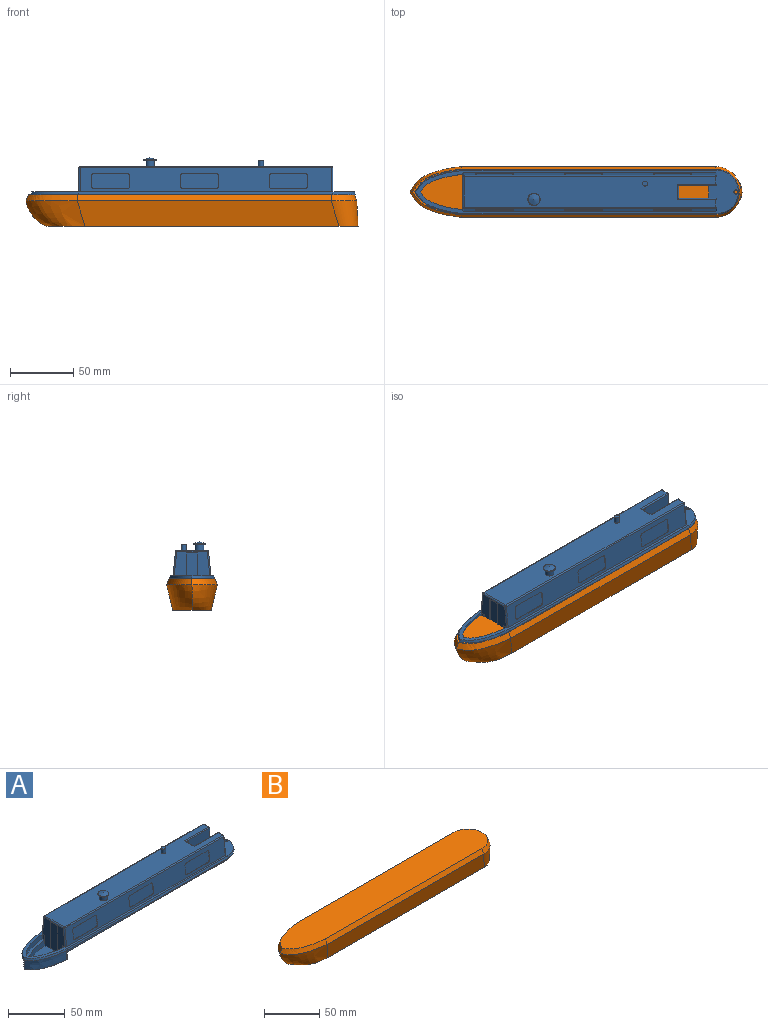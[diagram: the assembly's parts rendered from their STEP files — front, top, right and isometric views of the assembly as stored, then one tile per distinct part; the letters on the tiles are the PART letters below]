
ASSEMBLY  parts=2 mates=1
PART A: 146 faces, bbox 258.2x37.5x42 mm
  f0: plane 214.33x14.24mm, normal (0,0,-1), area 43.4mm2, adj f37,f39,f111,f132,f136,f137
  f1: plane 214.36x14.27mm, normal (0,0,-1), area 43.2mm2, adj f38,f40,f111,f132,f134,f135
  f2: plane 198.05x19.1mm, normal (0,0.99,0.1), area 2766.1mm2, adj f11,f82,f83,f84,f85,f86,f87,f88
  f3: plane 198.05x19.1mm, normal (0,-0.99,0.1), area 2734.1mm2, adj f11,f55,f56,f57,f58,f59,f60,f61
  f4: plane 20x1.2mm, normal (-1,0,0), area 24mm2, adj f6,f36,f44,f52
  f5: plane 198.05x24.04mm, normal (0,0,1), area 4345.1mm2, adj f117,f122,f123,f127,f128,f129,f130,f131
  f6: plane 197.65x23.68mm, normal (0,0,-1), area 4327.5mm2, adj f4,f7,f35,f36,f41,f42,f43,f49
  f7: plane 20x1.2mm, normal (-1,0,0), area 24mm2, adj f6,f35,f44,f51
  f8: plane 19x8.91mm, normal (1,0,0), area 150.5mm2, adj f11,f36,f121,f127
  f9: plane 19x8.91mm, normal (1,0,0), area 150.5mm2, adj f11,f35,f124,f128
  f10: plane 30x27.99mm, normal (-1,0,0), area 473mm2, adj f11,f12,f22,f23,f112,f113,f114,f116
  f11: plane 254.58x34.49mm, normal (0,0,1), area 1551.4mm2, adj f2,f3,f8,f9,f10,f12,f22,f24
  f12: extruded ~29.98x11mm, area 198mm2, adj f10,f11,f22,f23,f30,f34
  f13: plane 256.13x35.95mm, normal (0,0,-1), area 894.4mm2, adj f14,f15,f16,f17,f18,f19,f24,f25
  f14: extruded ~36.01x16mm, area 451.2mm2, adj f13,f15,f19,f139
  f15: extruded ~36.01x16mm, area 451.2mm2, adj f13,f14,f16,f138
  f16: plane 199.94x11.11mm, normal (0,-1,0), area 607.9mm2, adj f13,f15,f17,f111,f135,f138
  f17: extruded ~15.98x15.13mm, area 72.8mm2, adj f13,f16,f132,f134
  f18: extruded ~15.98x15.13mm, area 72.8mm2, adj f13,f19,f132,f137
  f19: plane 199.94x11.11mm, normal (0,1,0), area 607.9mm2, adj f13,f14,f18,f111,f136,f139
  f20: plane 24.6x0.09mm, normal (0,0,-1), area 2.1mm2, adj f43,f45,f46,f111
  f21: plane 36.84x31.2mm, normal (0,0,-1), area 770.6mm2, adj f111,f138,f139
  f22: extruded ~29.98x11mm, area 198mm2, adj f10,f11,f12,f23,f31,f34
  f23: plane 30.48x21.91mm, normal (0,0,1), area 454.3mm2, adj f10,f12,f22,f112,f113,f115
  f24: plane 200.04x2mm, normal (0,0.95,0.32), area 421.7mm2, adj f11,f13,f25,f26
  f25: bspline ~18.01x18mm, area 57.4mm2, adj f11,f13,f24,f27
  f26: bspline ~41.47x20.63mm, area 90.8mm2, adj f11,f13,f24,f28
  f27: bspline ~18.01x18mm, area 57.4mm2, adj f11,f13,f25,f29
  f28: bspline ~41.47x20.63mm, area 90.8mm2, adj f11,f13,f26,f29
  f29: plane 200.04x2mm, normal (0,-0.95,0.32), area 421.7mm2, adj f11,f13,f27,f28
  f30: plane 5x3.02mm, normal (-1,0,0), area 15.1mm2, adj f11,f12,f33,f34
  f31: plane 5x3.02mm, normal (-1,0,0), area 15.1mm2, adj f11,f22,f32,f34
  f32: extruded ~33.25x13.94mm, area 186.5mm2, adj f11,f31,f33,f34
  f33: extruded ~33.25x13.94mm, area 186.5mm2, adj f11,f30,f32,f34
  f34: plane 33.25x27.88mm, normal (0,0,1), area 209mm2, adj f12,f22,f30,f31,f32,f33
  f35: plane 30x20.2mm, normal (0,-1,0), area 522.4mm2, adj f6,f7,f9,f11,f44,f53,f54,f130
  f36: plane 30x20.2mm, normal (0,1,0), area 522.4mm2, adj f4,f6,f8,f11,f44,f53,f54,f129
  f37: plane 199.19x4.8mm, normal (0,-1,0), area 956.1mm2, adj f0,f39,f44,f48,f109
  f38: plane 199.19x4.8mm, normal (0,1,0), area 956.1mm2, adj f1,f40,f44,f47,f110
  f39: extruded ~14.75x13.59mm, area 105.8mm2, adj f0,f37,f44,f132
  f40: extruded ~14.75x13.59mm, area 105.8mm2, adj f1,f38,f44,f132
  f41: plane 20x7.63mm, normal (-1,0,0), area 131.8mm2, adj f6,f44,f49,f52
  f42: plane 20x7.63mm, normal (-1,0,0), area 131.8mm2, adj f6,f44,f50,f51
  f43: plane 27.84x24.8mm, normal (1,0,0), area 633.2mm2, adj f6,f20,f44,f45,f46,f49,f50
  f44: plane 214.42x30.07mm, normal (0,0,-1), area 840.3mm2, adj f4,f7,f35,f36,f37,f38,f39,f40
  f45: extruded ~4.8x0.34mm, area 1.7mm2, adj f20,f43,f44,f47,f110
  f46: extruded ~4.8x0.34mm, area 1.7mm2, adj f20,f43,f44,f48,f109
  f47: plane 4.8x2.54mm, normal (1,0,0), area 12.2mm2, adj f38,f44,f45,f110
  f48: plane 4.8x2.54mm, normal (1,0,0), area 12.2mm2, adj f37,f44,f46,f109
  f49: plane 197.65x20mm, normal (0,0.99,-0.1), area 3974.3mm2, adj f6,f41,f43,f44
  f50: plane 197.65x20mm, normal (0,-0.99,-0.1), area 3974.3mm2, adj f6,f42,f43,f44
  f51: plane 25x20mm, normal (0,1,0), area 500mm2, adj f6,f7,f42,f44
  f52: plane 25x20mm, normal (0,-1,0), area 500mm2, adj f4,f6,f41,f44
  f53: plane 10.17x0.2mm, normal (1,0,0), area 2mm2, adj f6,f35,f36,f131
  f54: plane 10.17x1.2mm, normal (-1,0,0), area 12.2mm2, adj f11,f35,f36,f44
  f55: plane 8.01x1.32mm, normal (-1,0,0), area 4mm2, adj f3,f56,f62,f63
  f56: cylinder r=2mm len=2.04mm, axis (0,-0.99,0.1), area 1.6mm2, adj f3,f55,f57,f63
  f57: plane 26x0.5mm, normal (0,-0.1,-0.99), area 13mm2, adj f3,f56,f58,f63
  f58: cylinder r=2mm len=2.04mm, axis (0,-0.99,0.1), area 1.6mm2, adj f3,f57,f59,f63
  f59: plane 8.01x1.32mm, normal (1,0,0), area 4mm2, adj f3,f58,f60,f63
  f60: cylinder r=2mm len=2.04mm, axis (0,-0.99,0.1), area 1.6mm2, adj f3,f59,f61,f63
  f61: plane 26x0.5mm, normal (0,0.1,0.99), area 13mm2, adj f3,f60,f62,f63
  f62: cylinder r=2mm len=2.04mm, axis (0,-0.99,0.1), area 1.6mm2, adj f3,f55,f61,f63
  f63: plane 30x11.94mm, normal (0,-0.99,0.1), area 356.6mm2, adj f55,f56,f57,f58,f59,f60,f61,f62
  f64: plane 8.01x1.32mm, normal (-1,0,0), area 4mm2, adj f3,f65,f71,f72
  f65: cylinder r=2mm len=2.04mm, axis (0,-0.99,0.1), area 1.6mm2, adj f3,f64,f66,f72
  f66: plane 26x0.5mm, normal (0,-0.1,-0.99), area 13mm2, adj f3,f65,f67,f72
  f67: cylinder r=2mm len=2.04mm, axis (0,-0.99,0.1), area 1.6mm2, adj f3,f66,f68,f72
  f68: plane 8.01x1.32mm, normal (1,0,0), area 4mm2, adj f3,f67,f69,f72
  f69: cylinder r=2mm len=2.04mm, axis (0,-0.99,0.1), area 1.6mm2, adj f3,f68,f70,f72
  f70: plane 26x0.5mm, normal (0,0.1,0.99), area 13mm2, adj f3,f69,f71,f72
  f71: cylinder r=2mm len=2.04mm, axis (0,-0.99,0.1), area 1.6mm2, adj f3,f64,f70,f72
  f72: plane 30x11.94mm, normal (0,-0.99,0.1), area 356.6mm2, adj f64,f65,f66,f67,f68,f69,f70,f71
  f73: plane 8.01x1.32mm, normal (-1,0,0), area 4mm2, adj f3,f74,f80,f81
  f74: cylinder r=2mm len=2.04mm, axis (0,-0.99,0.1), area 1.6mm2, adj f3,f73,f75,f81
  f75: plane 26x0.5mm, normal (0,-0.1,-0.99), area 13mm2, adj f3,f74,f76,f81
  f76: cylinder r=2mm len=2.04mm, axis (0,-0.99,0.1), area 1.6mm2, adj f3,f75,f77,f81
  f77: plane 8.01x1.32mm, normal (1,0,0), area 4mm2, adj f3,f76,f78,f81
  f78: cylinder r=2mm len=2.04mm, axis (0,-0.99,0.1), area 1.6mm2, adj f3,f77,f79,f81
  f79: plane 26x0.5mm, normal (0,0.1,0.99), area 13mm2, adj f3,f78,f80,f81
  f80: cylinder r=2mm len=2.04mm, axis (0,-0.99,0.1), area 1.6mm2, adj f3,f73,f79,f81
  f81: plane 30x11.94mm, normal (0,-0.99,0.1), area 356.6mm2, adj f73,f74,f75,f76,f77,f78,f79,f80
  f82: extruded ~2.01x2mm, area 1.9mm2, adj f2,f83,f89,f90
  f83: plane 7.75x1.4mm, normal (-1,0,0), area 4.6mm2, adj f2,f82,f84,f90
  f84: extruded ~2.01x2mm, area 1.9mm2, adj f2,f83,f85,f90
  f85: plane 26x0.6mm, normal (0,-0.1,0.99), area 15.6mm2, adj f2,f84,f86,f90
  f86: extruded ~2.01x2mm, area 1.9mm2, adj f2,f85,f87,f90
  f87: plane 7.75x1.4mm, normal (1,0,0), area 4.6mm2, adj f2,f86,f88,f90
  f88: extruded ~2.01x2mm, area 1.9mm2, adj f2,f87,f89,f90
  f89: plane 26x0.6mm, normal (0,0.1,-0.99), area 15.6mm2, adj f2,f82,f88,f90
  f90: plane 30x11.58mm, normal (0,0.99,0.1), area 345.9mm2, adj f82,f83,f84,f85,f86,f87,f88,f89
  f91: plane 7.75x1.4mm, normal (-1,0,0), area 4.6mm2, adj f2,f92,f98,f99
  f92: extruded ~2.01x2mm, area 1.9mm2, adj f2,f91,f93,f99
  f93: plane 26x0.6mm, normal (0,-0.1,0.99), area 15.6mm2, adj f2,f92,f94,f99
  f94: extruded ~2.01x2mm, area 1.9mm2, adj f2,f93,f95,f99
  f95: plane 7.75x1.4mm, normal (1,0,0), area 4.6mm2, adj f2,f94,f96,f99
  f96: extruded ~2.01x2mm, area 1.9mm2, adj f2,f95,f97,f99
  f97: plane 26x0.6mm, normal (0,0.1,-0.99), area 15.6mm2, adj f2,f96,f98,f99
  f98: extruded ~2.01x2mm, area 1.9mm2, adj f2,f91,f97,f99
  f99: plane 30x11.58mm, normal (0,0.99,0.1), area 345.9mm2, adj f91,f92,f93,f94,f95,f96,f97,f98
  f100: plane 26x0.6mm, normal (0,-0.1,0.99), area 15.6mm2, adj f2,f101,f107,f108
  f101: extruded ~2.01x2mm, area 1.9mm2, adj f2,f100,f102,f108
  f102: plane 7.75x1.4mm, normal (1,0,0), area 4.6mm2, adj f2,f101,f103,f108
  f103: extruded ~2.01x2mm, area 1.9mm2, adj f2,f102,f104,f108
  f104: plane 26x0.6mm, normal (0,0.1,-0.99), area 15.6mm2, adj f2,f103,f105,f108
  f105: extruded ~2.01x2mm, area 1.9mm2, adj f2,f104,f106,f108
  f106: plane 7.75x1.4mm, normal (-1,0,0), area 4.6mm2, adj f2,f105,f107,f108
  f107: extruded ~2.01x2mm, area 1.9mm2, adj f2,f100,f106,f108
  f108: plane 30x11.58mm, normal (0,0.99,0.1), area 345.9mm2, adj f100,f101,f102,f103,f104,f105,f106,f107
  f109: plane 2.54x0.25mm, normal (0,0,1), area 0.6mm2, adj f37,f46,f48,f111
  f110: plane 2.54x0.25mm, normal (0,0,1), area 0.6mm2, adj f38,f45,f47,f111
  f111: plane 32x9mm, normal (1,0,0), area 256.2mm2, adj f0,f1,f16,f19,f20,f21,f109,f110
  f112: plane 29.11x0.5mm, normal (0,-1,0), area 14.6mm2, adj f10,f23,f114,f115
  f113: plane 29.11x0.5mm, normal (0,1,0), area 14.6mm2, adj f10,f23,f114,f115
  f114: plane 9.01x0.5mm, normal (0,0,-1), area 4.5mm2, adj f10,f112,f113,f115
  f115: plane 29.11x9.01mm, normal (-1,0,0), area 262.3mm2, adj f23,f112,f113,f114
  f116: cylinder r=1mm len=19.21mm, axis (0,0.1,0.99), area 30.1mm2, adj f3,f10,f11,f119
  f117: cylinder r=1mm len=24.04mm, axis (0,1,0), area 37.8mm2, adj f5,f10,f119,f120
  f118: cylinder r=1mm len=19.21mm, axis (0,0.1,-0.99), area 30.1mm2, adj f2,f10,f11,f120
  f119: sphere r=1mm, area 1.5mm2, adj f116,f117,f122
  f120: sphere r=1mm, area 2mm2, adj f117,f118,f123
  f121: cylinder r=1mm len=19.21mm, axis (0,-0.1,-0.99), area 30.1mm2, adj f3,f8,f11,f125
  f122: cylinder r=1mm len=198.05mm, axis (-1,0,0), area 290.6mm2, adj f3,f5,f119,f125
  f123: cylinder r=1mm len=198.05mm, axis (1,0,0), area 290.6mm2, adj f2,f5,f120,f126
  f124: cylinder r=1mm len=19.21mm, axis (0,-0.1,0.99), area 30.1mm2, adj f2,f9,f11,f126
  f125: sphere r=1mm, area 1.5mm2, adj f121,f122,f127
  f126: sphere r=1mm, area 1mm2, adj f123,f124,f128
  f127: cylinder r=1mm len=6.93mm, axis (0,-1,0), area 10.1mm2, adj f5,f8,f125,f129
  f128: cylinder r=1mm len=6.93mm, axis (0,-1,0), area 10.1mm2, adj f5,f9,f126,f130
  f129: cylinder r=1mm len=31mm, axis (-1,0,0), area 47.1mm2, adj f5,f36,f127,f131
  f130: cylinder r=1mm len=31mm, axis (1,0,0), area 47.1mm2, adj f5,f35,f128,f131
  f131: cylinder r=1mm len=12.17mm, axis (0,1,0), area 17.6mm2, adj f5,f53,f129,f130
  f132: cylinder r=1.25mm len=6.42mm, axis (0,0,1), area 25.8mm2, adj f0,f1,f13,f17,f18,f39,f40,f44
  f133: cone r=0.67mm half-angle=45deg, axis (0,0,-1), area 5.4mm2, adj f11,f132
  f134: bspline ~16.31x16.04mm, area 32.9mm2, adj f1,f17,f132,f135
  f135: plane 198.94x1mm, normal (0,-0.71,-0.71), area 281.3mm2, adj f1,f16,f111,f134
  f136: plane 198.94x1mm, normal (0,0.71,-0.71), area 281.3mm2, adj f0,f19,f111,f137
  f137: bspline ~16.31x16.04mm, area 32.9mm2, adj f0,f18,f132,f136
  f138: bspline ~37.11x16.6mm, area 58.2mm2, adj f15,f16,f21,f111,f139
  f139: bspline ~37.11x16.6mm, area 58.2mm2, adj f14,f19,f21,f111,f138
  f140: cylinder r=2mm len=5mm, axis (0,0,-1), area 62.8mm2, adj f5,f141
  f141: plane 4x4mm, normal (0,0,1), area 12.6mm2, adj f140
  f142: cylinder r=3.5mm len=7mm, axis (0,0,-1), area 110mm2, adj f5,f143
  f143: plane 9.12x9.12mm, normal (0,0,-1), area 26.9mm2, adj f142,f145
  f144: cone r=0mm half-angle=73.4deg, axis (0,0,-1), area 70.8mm2, adj f145
  f145: torus R=4.56mm, axis (0,0,-1), area 25.6mm2, adj f143,f144
PART B: 12 faces, bbox 262x40.5x25.5 mm
  f0: plane 245.55x30.55mm, normal (0,0,-1), area 7033.4mm2, adj f1,f2,f3,f4,f5
  f1: bspline ~46.5x20mm, area 966.9mm2, adj f0,f2,f5,f7
  f2: plane 206.16x20mm, normal (0,0.97,-0.24), area 4124.8mm2, adj f0,f1,f3,f11
  f3: bspline ~221.16x40mm, area 1106.1mm2, adj f0,f2,f4,f10
  f4: plane 206.16x20mm, normal (0,-0.97,-0.24), area 4124.8mm2, adj f0,f3,f5,f9
  f5: bspline ~46.5x20mm, area 966.9mm2, adj f0,f1,f4,f8
  f6: plane 256.75x36.52mm, normal (0,0,1), area 8698.9mm2, adj f7,f8,f9,f10,f11
  f7: bspline ~40.45x20mm, area 246mm2, adj f1,f6,f8,f11
  f8: bspline ~40.45x20mm, area 246mm2, adj f5,f6,f7,f9
  f9: plane 200.16x5mm, normal (0,-0.93,0.37), area 1077.6mm2, adj f4,f6,f8,f10
  f10: bspline ~220.16x40mm, area 321.4mm2, adj f3,f6,f9,f11
  f11: plane 200.16x5mm, normal (0,0.93,0.37), area 1077.6mm2, adj f2,f6,f7,f10
PLACE A t=(33.3,37.36,-8.16)mm
PLACE B t=(56.66,37.35,-33.16)mm fixed
MATE parallel A.f13 <-> B.f6  axis (0,0,-1) through (43.82,37.35,-8.16)mm
